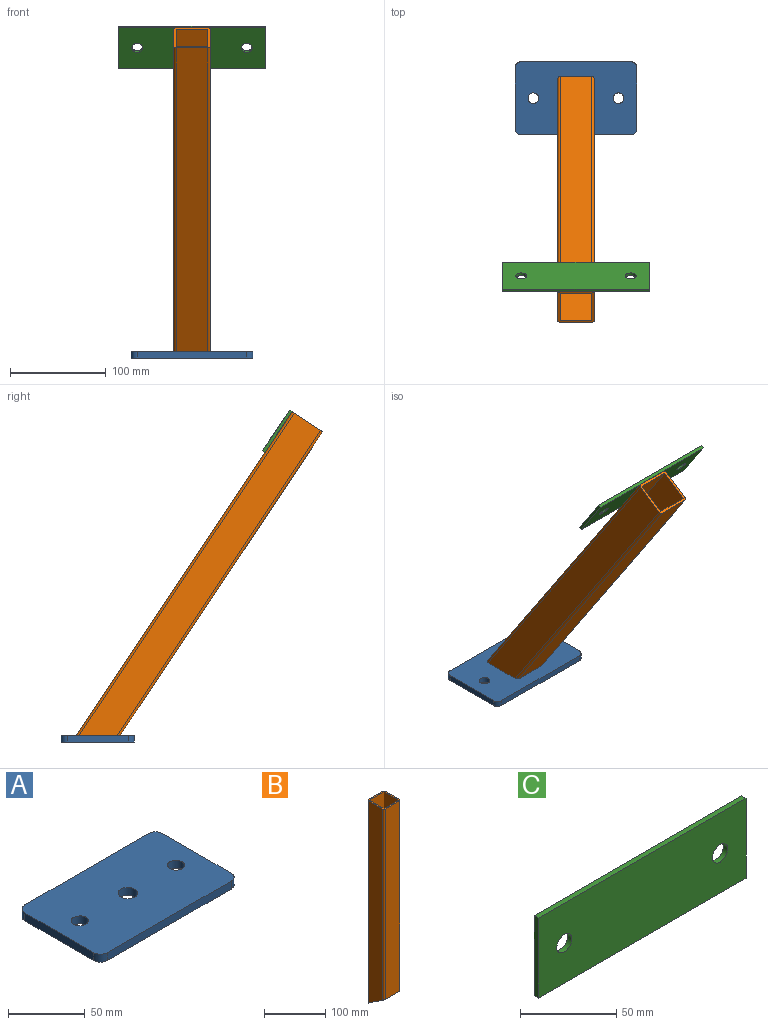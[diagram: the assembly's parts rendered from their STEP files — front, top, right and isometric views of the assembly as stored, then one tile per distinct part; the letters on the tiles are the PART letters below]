
ASSEMBLY  parts=3 mates=2
PART A: 13 faces, bbox 127x76.2x6.4 mm
  f0: plane 127x76.2mm, normal (0,0,-1), area 9322.1mm2, adj f2,f3,f4,f5,f6,f7,f8,f9
  f1: plane 127x76.2mm, normal (0,0,1), area 9322.1mm2, adj f2,f3,f4,f5,f6,f7,f8,f9
  f2: plane 114.3x6.35mm, normal (0,1,0), area 725.8mm2, adj f0,f1,f8,f11
  f3: plane 63.5x6.35mm, normal (-1,0,0), area 403.2mm2, adj f0,f1,f8,f9
  f4: plane 114.3x6.35mm, normal (0,-1,0), area 725.8mm2, adj f0,f1,f9,f10
  f5: plane 63.5x6.35mm, normal (1,0,0), area 403.2mm2, adj f0,f1,f10,f11
  f6: cylinder r=5.56mm len=11.11mm, axis (0,0,1), area 221.7mm2, adj f0,f1
  f7: cylinder r=5.56mm len=11.11mm, axis (0,0,1), area 221.7mm2, adj f0,f1
  f8: cylinder r=6.35mm len=6.35mm, axis (0,0,-1), area 63.3mm2, adj f0,f1,f2,f3
  f9: cylinder r=6.35mm len=6.35mm, axis (0,0,1), area 63.3mm2, adj f0,f1,f3,f4
  f10: cylinder r=6.35mm len=6.35mm, axis (0,0,-1), area 63.3mm2, adj f0,f1,f4,f5
  f11: cylinder r=6.35mm len=6.35mm, axis (0,0,1), area 63.3mm2, adj f0,f1,f2,f5
  f12: cylinder r=6.35mm len=12.7mm, axis (0,0,1), area 253.4mm2, adj f0,f1
PART B: 14 faces, bbox 38.1x38.1x406.4 mm
  f0: plane 404.71x33.02mm, normal (1,0,0), area 13000mm2, adj f8,f9,f12,f13
  f1: plane 404.71x33.02mm, normal (-1,0,0), area 13000mm2, adj f8,f9,f10,f11
  f2: plane 404.71x33.02mm, normal (1,0,0), area 13000mm2, adj f3,f5,f8,f9
  f3: plane 404.71x33.02mm, normal (0,-1,0), area 13363.4mm2, adj f2,f4,f8,f9
  f4: plane 404.71x33.02mm, normal (-1,0,0), area 13000mm2, adj f3,f5,f8,f9
  f5: plane 382.69x33.02mm, normal (0,1,0), area 12636.5mm2, adj f2,f4,f8,f9
  f6: plane 406.4x33.02mm, normal (0,1,0), area 13419.3mm2, adj f8,f9,f10,f13
  f7: plane 381x33.02mm, normal (0,-1,0), area 12580.6mm2, adj f8,f9,f11,f12
  f8: plane 38.1x38.1mm, normal (0,0,1), area 355.8mm2, adj f0,f1,f2,f3,f4,f5,f6,f7
  f9: plane 38.1x38.1mm, normal (0,-0.55,-0.83), area 427.6mm2, adj f0,f1,f2,f3,f4,f5,f6,f7
  f10: cylinder r=2.54mm len=406.4mm, axis (0,0,1), area 1619mm2, adj f1,f6,f8,f9
  f11: cylinder r=2.54mm len=382.69mm, axis (0,0,-1), area 1522.6mm2, adj f1,f7,f8,f9
  f12: cylinder r=2.54mm len=382.69mm, axis (0,0,1), area 1522.6mm2, adj f0,f7,f8,f9
  f13: cylinder r=2.54mm len=406.4mm, axis (0,0,-1), area 1619mm2, adj f0,f6,f8,f9
PART C: 8 faces, bbox 152.4x3.2x50.8 mm
  f0: plane 152.4x50.8mm, normal (0,1,0), area 7547.9mm2, adj f2,f3,f4,f5,f6,f7
  f1: plane 152.4x50.8mm, normal (0,-1,0), area 7547.9mm2, adj f2,f3,f4,f5,f6,f7
  f2: plane 152.4x3.18mm, normal (0,0,1), area 483.9mm2, adj f0,f1,f3,f5
  f3: plane 50.8x3.18mm, normal (-1,0,0), area 161.3mm2, adj f0,f1,f2,f4
  f4: plane 152.4x3.18mm, normal (0,0,-1), area 483.9mm2, adj f0,f1,f3,f5
  f5: plane 50.8x3.18mm, normal (1,0,0), area 161.3mm2, adj f0,f1,f2,f4
  f6: cylinder r=5.56mm len=11.11mm, axis (0,-1,0), area 110.8mm2, adj f0,f1
  f7: cylinder r=5.56mm len=11.11mm, axis (0,-1,0), area 110.8mm2, adj f0,f1
PLACE A at identity
PLACE B rot(axis=(1,0,0),33.7deg) t=(0,7.01,-10.57)mm
PLACE C rot(axis=(1,0,0),33.7deg) t=(0,-188.48,317.01)mm
MATE fastened B.f9 <-> A.f1  axis (0,0,-1) through (0,22.86,0)mm
MATE fastened C.f1 <-> B.f6  axis (0,-0.83,-0.55) through (0,-202.57,338.15)mm
